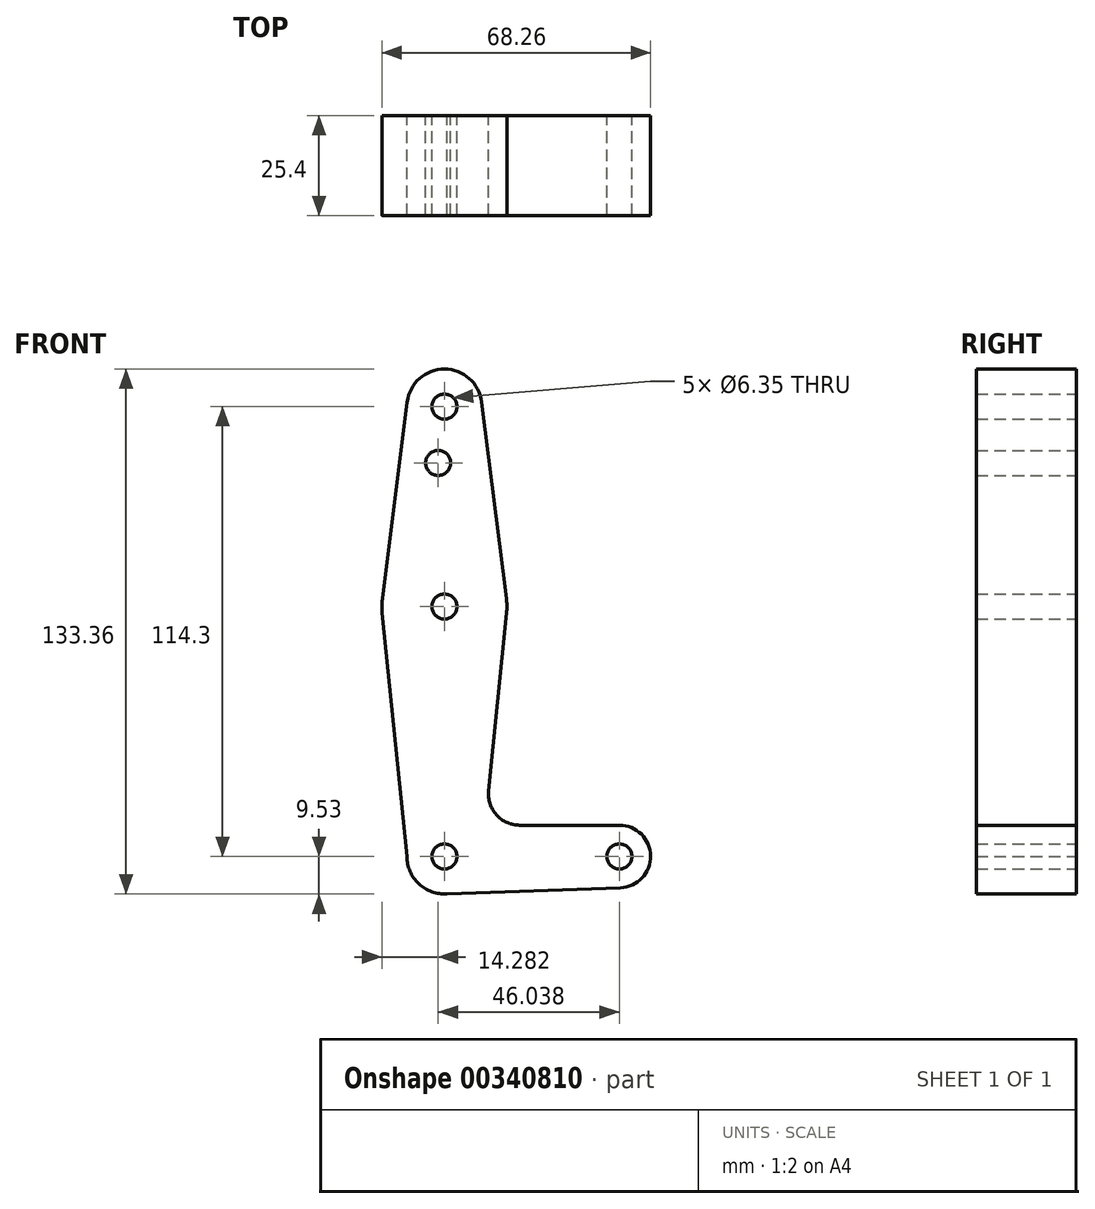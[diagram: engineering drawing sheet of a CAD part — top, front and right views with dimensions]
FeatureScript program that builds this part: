
annotation { "Feature Type Name" : "Feature", "Feature Type Description" : "" }
export const myFeature = defineFeature(function(context is Context, id is Id, definition is map)
    precondition{}
    {
        {
            var Q0;
            Q0=qCreatedBy(makeId("Front.planeOp"),FACE);
            var sketch = newSketch(context, id + "F0", { "sketchPlane" : qUnion([Q0])});
            skLineSegment(sketch, "E0", {"start": v(0, 0) * mm, "end": v(0, 114.3) * mm, "construction": true});
            skLineSegment(sketch, "E1", {"start": v(0, 0) * mm, "end": v(44.45, 0) * mm, "construction": true});
            skCircle(sketch, "E2", {"center": v(0, 114.3) * mm, "radius": 9.53 * mm});
            skCircle(sketch, "E3", {"center": v(0, 0) * mm, "radius": 9.53 * mm});
            skCircle(sketch, "E4", {"center": v(44.45, 0) * mm, "radius": 7.94 * mm});
            skLineSegment(sketch, "E5", {"start": v(-9.45, 115.5) * mm, "end": v(-15.75, 65.48) * mm});
            skLineSegment(sketch, "E6", {"start": v(9.45, 115.5) * mm, "end": v(15.75, 65.48) * mm});
            skLineSegment(sketch, "E7", {"start": v(0, -9.53) * mm, "end": v(44.73, -7.93) * mm});
            skCircle(sketch, "E8", {"center": v(0, 63.5) * mm, "radius": 15.88 * mm});
            skLineSegment(sketch, "E9", {"start": v(-15.8, 61.9) * mm, "end": v(-9.52, 0) * mm});
            skLineSegment(sketch, "E10", {"start": v(15.8, 61.9) * mm, "end": v(11.22, 16.69) * mm});
            skLineSegment(sketch, "E11", {"start": v(19.12, 7.94) * mm, "end": v(44.45, 7.94) * mm});
            skArc(sketch, "E12.filletArc", {"start": v(11.22, 16.69) * mm, "mid": v(13.23, 10.56) * mm, "end": v(19.12, 7.94) * mm});
            skCircle(sketch, "E13", {"center": v(0, 114.3) * mm, "radius": 3.18 * mm});
            skCircle(sketch, "E14", {"center": v(0, 63.5) * mm, "radius": 3.18 * mm});
            skCircle(sketch, "E15", {"center": v(-1.59, 100) * mm, "radius": 3.18 * mm});
            skCircle(sketch, "E16", {"center": v(0, 0) * mm, "radius": 3.18 * mm});
            skCircle(sketch, "E17", {"center": v(44.45, 0) * mm, "radius": 3.18 * mm});
            skSolve(sketch);
        }
        {
            var Q0;
            Q0 = qSketchRegion(id + "F0", true);
            extrude(context, id + "F1", {"entities" : qUnion([Q0]), "depth" : 25.4 * mm});
        }
    });
